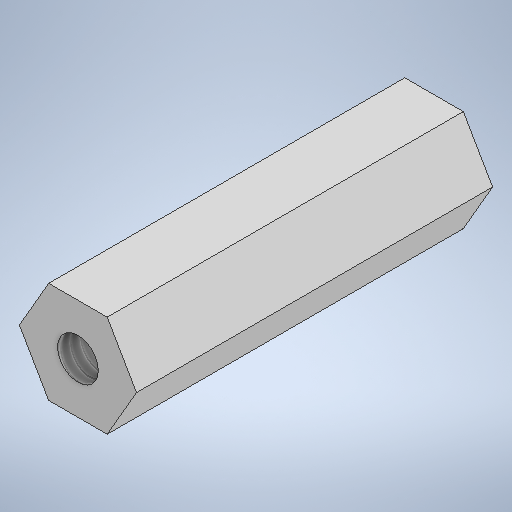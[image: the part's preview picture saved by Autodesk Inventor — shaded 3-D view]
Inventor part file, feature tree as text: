
AUTODESK INVENTOR PART (.ipt)
format: ipt  version: 2025.1 (Build 291241020, 241B)  size: 222,208 bytes
history: native  units: in
note: dims shown in document units (in); Inventor stores cm internally (conversion verified against a paired STEP export)
features: extrude x1, thread x1, sketch x1
ambient origin geometry x8: Origin, YZ Plane, XZ Plane, XY Plane, X Axis, Y Axis, Z Axis, Center Point
bodies: Solid1 (feature_tree)
feature tree (3):
  extrude  "Extrusion1"  Depth=0.5in
  thread  "Thread1"  [1 undecoded]
  sketch  "Sketch1"  dims[d0=0.201in d1=0.5in d2=1.756in d3=0.0in d4=1.756in d5=0.0in]
note: 1 required parameter value undecoded (feature->parameter linkage not recoverable at this tier; creation-order binding heuristic only, values carry confidence <= 0.55)
